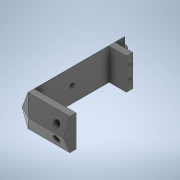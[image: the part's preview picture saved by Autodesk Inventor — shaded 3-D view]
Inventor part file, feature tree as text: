
AUTODESK INVENTOR PART (.ipt)
format: ipt  version: 2020 (Build 240168000, 168)  size: 360,960 bytes
history: native  units: in
note: dims shown in document units (in); Inventor stores cm internally (conversion verified against a paired STEP export)
features: sketch x16, extrude x11, plane x6, projected_geometry x6, loft x2, other x1
ambient origin geometry x8: Origin, YZ Plane, XZ Plane, XY Plane, X Axis, Y Axis, Z Axis, Center Point
bodies: Solid1 (feature_tree)
feature tree (42):
  sketch  "Sketch1"  dims[d1=1.1811in d2=3.5827in]
  plane  "Work Plane1"
  loft  "Loft1"
  extrude  "Extrusion1"  Depth=0.5906in
  extrude  "Extrusion2"  TaperAngle=0.0deg  [1 undecoded]
  extrude  "Extrusion3"  Depth=0.2362in
  extrude  "Extrusion4"  Depth=0.315in
  extrude  "Extrusion5"  TaperAngle=0.0deg  [1 undecoded]
  extrude  "Extrusion6"  TaperAngle=0.0deg  [1 undecoded]
  extrude  "Extrusion8"  Depth=0.315in
  sketch  "Sketch13"  dims[d24=0.0in d25=0.1181in]
  plane  "Work Plane2"
  plane  "Work Plane8"
  sketch  "Sketch14"  dims[d26=0.1181in d27=0.2362in]
  loft  "Loft2"
  sketch  "Sketch15"  dims[d28=0.2362in d29=0.1142in]
  extrude  "Extrusion9"  Depth=0.1181in
  plane  "Work Plane3"
  sketch  "Sketch18"  dims[d32=0.0in]
  plane  "Work Plane5"
  plane  "Work Plane7"
  extrude  "Extrusion10"  Depth=0.2362in
  extrude  "Extrusion11"  Depth=0.1142in
  extrude  "Extrusion12"  Depth=0.2756in
  sketch  "Sketch2"  dims[d3=1.1811in d5=0.5906in]
  sketch  "Sketch3"  dims[d6=0.5906in d7=0.0in d8=90.0deg]
  sketch  "Sketch4"  dims[d9=0.0in d10=90.0deg d11=0.2362in]
  sketch  "Sketch5"  dims[d12=0.2362in d13=0.315in]
  projected_geometry  "Projected Loop1"
  sketch  "Sketch6"  dims[d14=0.65in d15=0.0in]
  projected_geometry  "Projected Loop2"
  sketch  "Sketch8"  dims[d17=0.1654in d18=0.0in d19=0.0in]
  sketch  "Sketch9"  dims[d20=0.1575in d21=0.315in]
  projected_geometry  "Projected Loop6"
  sketch  "Sketch11"  dims[d22=0.0in d23=0.9055in]
  projected_geometry  "Projected Loop8"
  projected_geometry  "Projected Loop9"
  other  "Edges1"
  projected_geometry  "Projected Loop10"
  sketch  "Sketch17"  dims[d30=0.1142in d31=0.2756in]
  sketch  "Sketch19"  dims[d41=0.2756in d42=0.0in]
  sketch  "Sketch20"  dims[d48=0.1181in d49=0.1181in d50=0.0157in d51=0.5906in d52=0.0157in d53=0.2362in d56=0.122in d57=0.3543in d58=0.122in d59=0.3543in d60=1.2012in d61=1.2012in d62=0.2402in d63=0.2402in d64=0.0906in d65=-0.2061in d66=-0.0206in d67=0.0in d68=90.0deg d69=0.0in d70=90.0deg d71=1.9488in d72=0.2362in d73=0.3937in d74=0.0in d75=0.2362in d76=0.0884in d77=0.0in d78=0.3937in d79=0.0in d80=0.3937in d81=0.0in d82=0.0394in d4=0.0197in]
note: 3 required parameter values undecoded (feature->parameter linkage not recoverable at this tier; creation-order binding heuristic only, values carry confidence <= 0.55)
